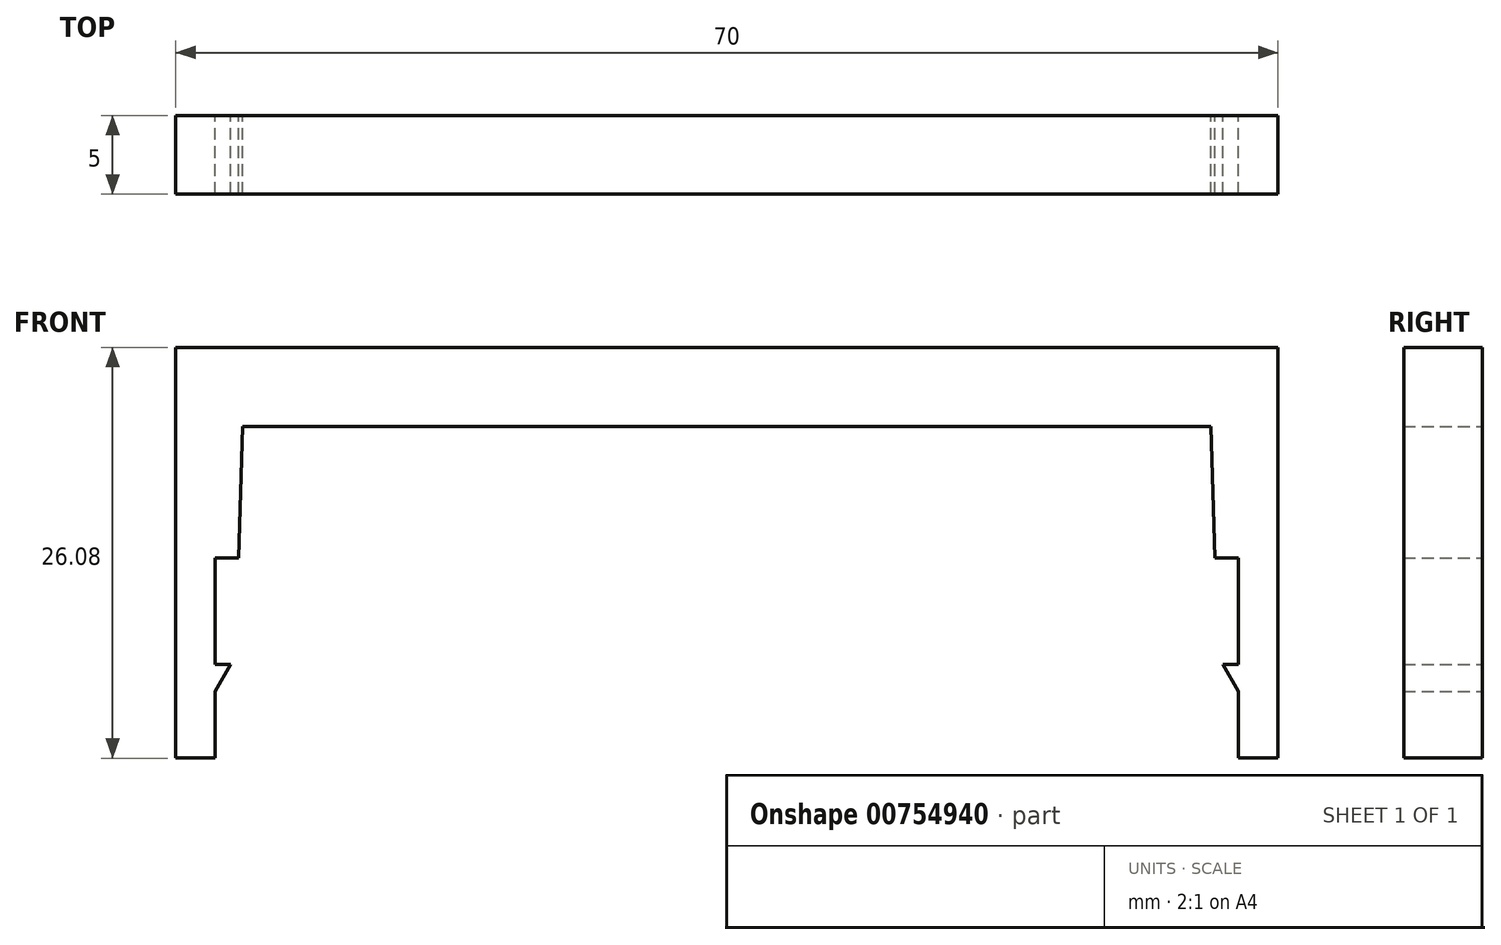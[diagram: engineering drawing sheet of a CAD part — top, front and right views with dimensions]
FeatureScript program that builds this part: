
annotation { "Feature Type Name" : "Feature", "Feature Type Description" : "" }
export const myFeature = defineFeature(function(context is Context, id is Id, definition is map)
    precondition{}
    {
        {
            var Q0;
            Q0=qCreatedBy(makeId("Front.planeOp"),FACE);
            var sketch = newSketch(context, id + "F0", { "sketchPlane" : qUnion([Q0])});
            skLineSegment(sketch, "E0", {"start": v(-35, -21.08) * mm, "end": v(-35, 5) * mm});
            skLineSegment(sketch, "E1", {"start": v(-35, 5) * mm, "end": v(0, 5) * mm});
            skLineSegment(sketch, "E2", {"start": v(-32.5, -16.83) * mm, "end": v(-31.5, -15.13) * mm});
            skLineSegment(sketch, "E3", {"start": v(-31.5, -15.13) * mm, "end": v(-32.5, -15.13) * mm});
            skLineSegment(sketch, "E4", {"start": v(-32.5, -15.13) * mm, "end": v(-32.5, -8.38) * mm});
            skLineSegment(sketch, "E5", {"start": v(-30.75, 0) * mm, "end": v(0, 0) * mm});
            skLineSegment(sketch, "E6", {"start": v(-32.5, -8.38) * mm, "end": v(-31, -8.38) * mm});
            skLineSegment(sketch, "E7", {"start": v(-31, -8.38) * mm, "end": v(-30.75, 0) * mm});
            skLineSegment(sketch, "E8.MirrorCS", {"start": v(30.75, 0) * mm, "end": v(0, 0) * mm});
            skLineSegment(sketch, "E9.MirrorCS", {"start": v(35, 5) * mm, "end": v(0, 5) * mm});
            skLineSegment(sketch, "E10.MirrorCS", {"start": v(31.5, -15.13) * mm, "end": v(32.5, -15.13) * mm});
            skLineSegment(sketch, "E11.MirrorCS", {"start": v(32.5, -8.38) * mm, "end": v(31, -8.38) * mm});
            skLineSegment(sketch, "E12.MirrorCS", {"start": v(32.5, -16.83) * mm, "end": v(31.5, -15.13) * mm});
            skLineSegment(sketch, "E13.MirrorCS", {"start": v(32.5, -15.13) * mm, "end": v(32.5, -8.38) * mm});
            skLineSegment(sketch, "E14.MirrorCS", {"start": v(31, -8.38) * mm, "end": v(30.75, 0) * mm});
            skLineSegment(sketch, "E15.MirrorCS", {"start": v(35, -21.08) * mm, "end": v(35, 5) * mm});
            skLineSegment(sketch, "E16", {"start": v(-32.5, -16.83) * mm, "end": v(-32.5, -21.08) * mm});
            skLineSegment(sketch, "E17", {"start": v(-32.5, -21.08) * mm, "end": v(-35, -21.08) * mm});
            skLineSegment(sketch, "E18", {"start": v(-35, -21.08) * mm, "end": v(-35, -21.08) * mm});
            skLineSegment(sketch, "E19.MirrorCS", {"start": v(32.5, -16.83) * mm, "end": v(32.5, -21.08) * mm});
            skLineSegment(sketch, "E20.MirrorCS", {"start": v(35, -21.08) * mm, "end": v(35, -21.08) * mm});
            skLineSegment(sketch, "E21.MirrorCS", {"start": v(32.5, -21.08) * mm, "end": v(35, -21.08) * mm});
            skSolve(sketch);
        }
        {
            var Q0;
            Q0=makeQuery(id+"F0.imprint","IMPRINT",FACE,{"disambiguationData":[TD([[makeQuery(id+"F0.imprint","IMPRINT",EDGE,{"derivedFrom":sQuery(id+"F0.wireOp",EDGE,"E0")}),-1.0]])]});
            extrude(context, id + "F1", {"entities" : qUnion([Q0]), "depth" : 5 * mm, "offsetDistance" : 25.4 * mm});
        }
    });
